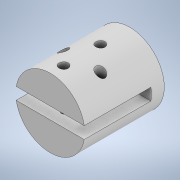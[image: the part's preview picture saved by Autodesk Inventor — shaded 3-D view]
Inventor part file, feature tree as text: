
AUTODESK INVENTOR PART (.ipt)
format: ipt  version: 2022 (Build 260153000, 153)  size: 194,048 bytes
history: native  units: mm
features: extrude x6, sketch x6, plane x2
ambient origin geometry x8: Origin, YZ Plane, XZ Plane, XY Plane, X Axis, Y Axis, Z Axis, Center Point
bodies: Solid1 (feature_tree)
feature tree (14):
  extrude  "Extrusion1"  Depth=3.25mm
  extrude  "Extrusion2"  Depth=31.2mm TaperAngle=0.0deg
  plane  "Work Plane1"
  sketch  "Sketch3"  dims[d8=2.5mm d10=40.0mm d12=360.0deg]
  plane  "Work Plane2"
  extrude  "Extrusion3"  Depth=2.5mm TaperAngle=360.0deg
  sketch  "Sketch4"  dims[d14=31.2mm d15=0.0mm d16=5.0mm]
  extrude  "Extrusion4"  Depth=5.0mm
  extrude  "Extrusion5"  Depth=5.0mm TaperAngle=0.0deg
  extrude  "Extrusion6"  Depth=6.2mm
  sketch  "Sketch1"  dims[d1=7.0mm d2=0.0mm d3=3.25mm]
  sketch  "Sketch2"  dims[d4=3.25mm d5=31.2mm d6=0.0mm]
  sketch  "Sketch5"  dims[d17=5.0mm d18=5.0mm d19=0.0mm]
  sketch  "Sketch6"  dims[d20=8.0mm d21=0.0mm d22=5.5mm d23=6.2mm d24=0.0mm]
